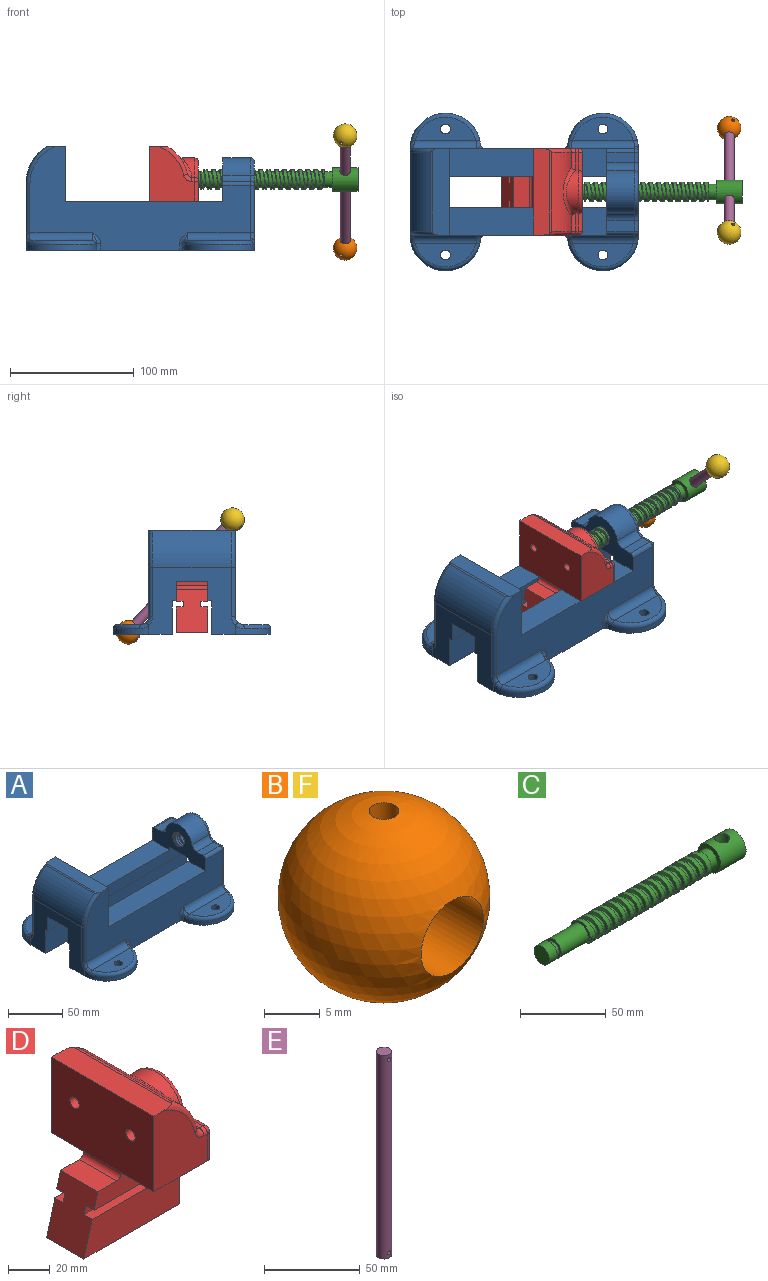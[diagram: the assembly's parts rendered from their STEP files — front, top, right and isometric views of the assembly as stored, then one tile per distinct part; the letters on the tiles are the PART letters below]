
ASSEMBLY  parts=6 mates=6
PART A: 90 faces, bbox 191.8x135.1x93.3 mm
  f0: plane 69.98x35.06mm, normal (-1,0,0), area 1390.7mm2, adj f1,f4,f6,f7,f9,f25,f26,f27
  f1: cylinder r=6.39mm len=25.4mm, axis (1,0,0), area 430.9mm2, adj f0,f5,f86,f88,f89
  f2: plane 184.15x47.6mm, normal (0,0,-1), area 5973.6mm2, adj f3,f5,f6,f11,f12,f14,f15,f29
  f3: plane 69.85x53.98mm, normal (-1,0,0), area 2224.7mm2, adj f2,f10,f11,f17,f24,f28,f29,f30
  f4: plane 127x22.2mm, normal (0,0,1), area 2819.3mm2, adj f0,f7,f23,f35
  f5: plane 71.56x69.98mm, normal (1,0,0), area 2448.5mm2, adj f1,f2,f10,f14,f20,f28,f29,f30
  f6: plane 181.19x87.52mm, normal (0,1,0), area 6838.3mm2, adj f0,f2,f8,f9,f23,f42,f45,f51
  f7: plane 181.19x87.52mm, normal (0,-1,0), area 6838.3mm2, adj f0,f4,f8,f10,f23,f43,f44,f46
  f8: plane 70.71x14.43mm, normal (0,0,1), area 942.4mm2, adj f6,f7,f23,f81,f83,f85
  f9: plane 127x22.2mm, normal (0,0,1), area 2819.3mm2, adj f0,f6,f23,f32
  f10: plane 184.15x47.6mm, normal (0,0,-1), area 5973.6mm2, adj f3,f5,f7,f17,f18,f20,f21,f28
  f11: cylinder r=28.57mm len=57.01mm, axis (0,0,-1), area 423.3mm2, adj f2,f3,f69,f71,f73,f75
  f12: cylinder r=3.96mm len=7.93mm, axis (0,0,-1), area 197.3mm2, adj f2,f13
  f13: plane 49.19x19.05mm, normal (0,0,1), area 644.9mm2, adj f12,f42,f73
  f14: cylinder r=28.57mm len=57.01mm, axis (0,0,-1), area 423.3mm2, adj f2,f5,f51,f56,f58,f60
  f15: cylinder r=3.96mm len=7.93mm, axis (0,0,-1), area 197.3mm2, adj f2,f16
  f16: plane 49.19x19.05mm, normal (0,0,1), area 644.9mm2, adj f15,f45,f58
  f17: cylinder r=28.57mm len=57.01mm, axis (0,0,-1), area 423.3mm2, adj f3,f10,f72,f76,f78,f80
  f18: cylinder r=3.96mm len=7.93mm, axis (0,0,-1), area 197.3mm2, adj f10,f19
  f19: plane 49.19x19.05mm, normal (0,0,1), area 644.9mm2, adj f18,f43,f78
  f20: cylinder r=28.57mm len=57.01mm, axis (0,0,-1), area 423.3mm2, adj f5,f10,f46,f48,f49,f50
  f21: cylinder r=3.96mm len=7.93mm, axis (0,0,-1), area 197.3mm2, adj f10,f22
  f22: plane 49.19x19.05mm, normal (0,0,1), area 644.9mm2, adj f21,f44,f49
  f23: plane 69.85x44.45mm, normal (1,0,0), area 2960.4mm2, adj f4,f6,f7,f8,f9,f32,f34,f35
  f24: cylinder r=34.92mm len=63.5mm, axis (0,-1,0), area 2251.5mm2, adj f3,f81,f83,f85
  f25: cylinder r=17.45mm len=34.2mm, axis (1,0,0), area 1062.5mm2, adj f0,f40,f41,f63
  f26: plane 22.23x8.43mm, normal (0,0,1), area 187.3mm2, adj f0,f41,f64,f68
  f27: plane 22.23x8.43mm, normal (0,0,1), area 187.3mm2, adj f0,f40,f55,f59
  f28: plane 184.15x26.97mm, normal (0,1,0), area 4967.4mm2, adj f3,f5,f10,f31
  f29: plane 184.15x26.97mm, normal (0,-1,0), area 4967.4mm2, adj f2,f3,f5,f30
  f30: plane 184.15x3.18mm, normal (0,0,-1), area 584.7mm2, adj f3,f5,f29,f32
  f31: plane 184.15x3.18mm, normal (0,0,-1), area 584.7mm2, adj f3,f5,f28,f35
  f32: plane 184.15x15.89mm, normal (0,-1,0), area 2520.9mm2, adj f0,f3,f5,f9,f23,f30,f33,f34
  f33: plane 25.45x25.4mm, normal (0,0,-1), area 646.5mm2, adj f0,f5,f32,f35
  f34: plane 31.75x25.45mm, normal (0,0,-1), area 808.1mm2, adj f3,f23,f32,f35
  f35: plane 184.15x15.89mm, normal (0,1,0), area 2520.9mm2, adj f0,f3,f4,f5,f23,f31,f33,f34
  f36: cylinder r=3.17mm len=15.88mm, axis (1,0,0), area 316.7mm2, adj f23,f37
  f37: plane 6.35x6.35mm, normal (1,0,0), area 31.7mm2, adj f36
  f38: cylinder r=3.17mm len=15.88mm, axis (1,0,0), area 316.7mm2, adj f23,f39
  f39: plane 6.35x6.35mm, normal (1,0,0), area 31.7mm2, adj f38
  f40: cylinder r=6.35mm len=22.23mm, axis (1,0,0), area 193.3mm2, adj f0,f25,f27,f61
  f41: cylinder r=6.35mm len=22.23mm, axis (1,0,0), area 193.3mm2, adj f0,f25,f26,f66
  f42: cylinder r=6.35mm len=50.6mm, axis (-1,0,0), area 499.8mm2, adj f6,f13,f71,f75,f77
  f43: cylinder r=6.35mm len=50.6mm, axis (1,0,0), area 499.8mm2, adj f7,f19,f76,f80,f82
  f44: cylinder r=6.35mm len=50.6mm, axis (1,0,0), area 499.8mm2, adj f7,f22,f48,f50,f52
  f45: cylinder r=6.35mm len=50.6mm, axis (-1,0,0), area 499.8mm2, adj f6,f16,f56,f60,f62
  f46: cylinder r=3.17mm len=5.55mm, axis (0,0,-1), area 25.9mm2, adj f7,f10,f20,f47
  f47: bspline ~10.3x6.39mm, area 17.6mm2, adj f7,f46,f48
  f48: bspline ~11.96x10.37mm, area 38.2mm2, adj f20,f44,f47,f49
  f49: torus R=25.4mm, axis (0,0,1), area 360.5mm2, adj f20,f22,f48,f50
  f50: bspline ~9.34x5.4mm, area 29.6mm2, adj f20,f44,f49,f52
  f51: cylinder r=3.17mm len=5.55mm, axis (0,0,-1), area 25.9mm2, adj f2,f6,f14,f53
  f52: torus R=9.53mm, axis (1,0,0), area 31.5mm2, adj f5,f44,f50,f54
  f53: bspline ~10.3x6.39mm, area 15.9mm2, adj f6,f51,f56
  f54: cylinder r=3.17mm len=38.1mm, axis (0,0,1), area 190mm2, adj f5,f7,f52,f57
  f55: cylinder r=3.17mm len=22.23mm, axis (-1,0,0), area 110.8mm2, adj f0,f7,f27,f57
  f56: bspline ~11.96x10.37mm, area 38.2mm2, adj f14,f45,f53,f58
  f57: sphere r=3.17mm, area 15.8mm2, adj f54,f55,f59
  f58: torus R=25.4mm, axis (0,0,1), area 360.5mm2, adj f14,f16,f56,f60
  f59: cylinder r=3.17mm len=8.43mm, axis (0,-1,0), area 42mm2, adj f5,f27,f57,f61
  f60: bspline ~9.34x5.4mm, area 29.6mm2, adj f14,f45,f58,f62
  f61: torus R=9.53mm, axis (1,0,0), area 51.3mm2, adj f5,f40,f59,f63
  f62: torus R=9.53mm, axis (1,0,0), area 31.5mm2, adj f5,f45,f60,f65
  f63: torus R=14.27mm, axis (1,0,0), area 222.7mm2, adj f5,f25,f61,f66
  f64: cylinder r=3.17mm len=22.23mm, axis (-1,0,0), area 110.8mm2, adj f0,f6,f26,f67
  f65: cylinder r=3.17mm len=38.1mm, axis (0,0,-1), area 190mm2, adj f5,f6,f62,f67
  f66: torus R=9.53mm, axis (1,0,0), area 51.3mm2, adj f5,f41,f63,f68
  f67: sphere r=3.17mm, area 10.1mm2, adj f64,f65,f68
  f68: cylinder r=3.17mm len=8.43mm, axis (0,-1,0), area 42mm2, adj f5,f26,f66,f67
  f69: cylinder r=3.17mm len=5.55mm, axis (0,0,-1), area 25.9mm2, adj f2,f6,f11,f70
  f70: bspline ~10.3x6.39mm, area 17.6mm2, adj f6,f69,f71
  f71: bspline ~11.96x10.37mm, area 38.2mm2, adj f11,f42,f70,f73
  f72: cylinder r=3.17mm len=5.55mm, axis (0,0,-1), area 25.9mm2, adj f7,f10,f17,f74
  f73: torus R=25.4mm, axis (0,0,1), area 360.5mm2, adj f11,f13,f71,f75
  f74: bspline ~10.3x6.39mm, area 15.9mm2, adj f7,f72,f76
  f75: bspline ~9.34x5.4mm, area 29.6mm2, adj f11,f42,f73,f77
  f76: bspline ~11.96x10.37mm, area 38.2mm2, adj f17,f43,f74,f78
  f77: torus R=9.53mm, axis (1,0,0), area 31.5mm2, adj f3,f42,f75,f79
  f78: torus R=25.4mm, axis (0,0,1), area 360.5mm2, adj f17,f19,f76,f80
  f79: cylinder r=3.17mm len=39.7mm, axis (0,0,1), area 198mm2, adj f3,f6,f77,f81
  f80: bspline ~9.34x5.4mm, area 29.6mm2, adj f17,f43,f78,f82
  f81: torus R=31.75mm, axis (0,1,0), area 187.9mm2, adj f6,f8,f24,f79,f83
  f82: torus R=9.53mm, axis (1,0,0), area 31.5mm2, adj f3,f43,f80,f84
  f83: cylinder r=3.17mm len=66.71mm, axis (0,-1,0), area 114.8mm2, adj f8,f24,f81,f85
  f84: cylinder r=3.17mm len=39.7mm, axis (0,0,-1), area 198mm2, adj f3,f7,f82,f85
  f85: torus R=31.75mm, axis (0,1,0), area 187.9mm2, adj f7,f8,f24,f83,f84
  f86: plane 1.76x1.55mm, normal (-0.13,-0.01,0.99), area 2.4mm2, adj f0,f1,f87,f89
  f87: cylinder r=7.94mm len=25.4mm, axis (-1,0,0), area 524.5mm2, adj f0,f5,f86,f88,f89
  f88: bspline ~26.93x18.32mm, area 290.1mm2, adj f0,f1,f5,f87
  f89: bspline ~24.81x18.34mm, area 272.9mm2, adj f1,f5,f86,f87
PART B: 5 faces, bbox 19.1x19.1x18.9 mm
  f0: sphere r=9.53mm, area 1077.6mm2, adj f1,f3,f4
  f1: cylinder r=3.96mm len=11.84mm, axis (0,-1,0), area 283.2mm2, adj f0,f2,f3,f4
  f2: plane 7.91x7.91mm, normal (0,-1,0), area 49.2mm2, adj f1
  f3: cylinder r=1.32mm len=5.7mm, axis (0,0,1), area 46.4mm2, adj f0,f1
  f4: cylinder r=1.32mm len=5.7mm, axis (0,0,1), area 46.4mm2, adj f0,f1
PART C: 21 faces, bbox 159.1x19.2x19.2 mm
  f0: cylinder r=9.53mm len=20.63mm, axis (-1,0,0), area 1111.2mm2, adj f18,f19,f20
  f1: plane 16.01x15.91mm, normal (1,0,0), area 53.5mm2, adj f2,f7,f8,f17
  f2: cylinder r=7.94mm len=100mm, axis (-1,0,0), area 3461mm2, adj f1,f3,f4,f6,f7,f8
  f3: plane 16.02x15.87mm, normal (-1,0,0), area 53.5mm2, adj f2,f4,f6,f10
  f4: plane 1.85x1.76mm, normal (0.13,0.01,-0.99), area 2.8mm2, adj f2,f3,f5,f8,f9
  f5: bspline ~103.1x14.08mm, area 1565.3mm2, adj f4,f6,f7,f8,f9,f16
  f6: bspline ~99.96x18.32mm, area 1318.7mm2, adj f2,f3,f5,f7,f9
  f7: plane 1.85x1.76mm, normal (-0.13,0.99,0), area 2.8mm2, adj f1,f2,f5,f6,f16
  f8: bspline ~99.96x18.34mm, area 1312.5mm2, adj f1,f2,f4,f5,f16
  f9: plane 6.27x5.25mm, normal (1,0,0), area 2.1mm2, adj f4,f5,f6,f10
  f10: cylinder r=6.35mm len=22.35mm, axis (1,0,0), area 891.8mm2, adj f3,f9,f11
  f11: plane 12.7x12.7mm, normal (-1,0,0), area 55.4mm2, adj f10,f12
  f12: cylinder r=4.76mm len=9.53mm, axis (1,0,0), area 98.8mm2, adj f11,f15
  f13: cylinder r=6.35mm len=12.7mm, axis (1,0,0), area 253.4mm2, adj f14,f15
  f14: plane 12.7x12.7mm, normal (-1,0,0), area 126.7mm2, adj f13
  f15: plane 12.7x12.7mm, normal (1,0,0), area 55.4mm2, adj f12,f13
  f16: plane 6.3x5.05mm, normal (-1,0,0), area 2.1mm2, adj f5,f7,f8,f17
  f17: cylinder r=6.35mm len=12.7mm, axis (-1,0,0), area 253.4mm2, adj f1,f16,f19
  f18: plane 19.05x19.05mm, normal (1,0,0), area 285mm2, adj f0
  f19: plane 19.05x19.05mm, normal (-1,0,0), area 158.3mm2, adj f0,f17
  f20: cylinder r=4.37mm len=19.05mm, axis (0,0,-1), area 522.6mm2, adj f0
PART D: 48 faces, bbox 65.9x70.7x89.2 mm
  f0: plane 14.38x2.42mm, normal (0,0,1), area 34.6mm2, adj f24,f32,f35,f37,f38
  f1: plane 70.71x14.43mm, normal (0,0,1), area 942.4mm2, adj f2,f4,f23,f36,f39,f42
  f2: plane 44.45x36.5mm, normal (0,1,0), area 1225.7mm2, adj f1,f17,f23,f42,f43,f45,f47
  f3: plane 69.82x63.5mm, normal (1,0,0), area 2160.8mm2, adj f5,f6,f7,f8,f9,f10,f11,f12
  f4: plane 44.45x36.5mm, normal (0,-1,0), area 1225.7mm2, adj f1,f5,f23,f31,f32,f33,f36
  f5: plane 39.68x22.23mm, normal (0,0,-1), area 879.6mm2, adj f3,f4,f6,f23,f31
  f6: plane 58.18x12.83mm, normal (0,-1,0), area 677mm2, adj f3,f5,f7,f20,f21,f22
  f7: plane 58.18x5.59mm, normal (0,0,-1), area 325.1mm2, adj f3,f6,f8,f20
  f8: plane 59.48x4.76mm, normal (0,-1,0), area 280.2mm2, adj f3,f7,f9,f20
  f9: plane 59.48x5.59mm, normal (0,0,1), area 332.4mm2, adj f3,f8,f10,f20
  f10: plane 65.08x20.51mm, normal (0,-1,0), area 1277.4mm2, adj f3,f9,f11,f20
  f11: plane 65.08x25.4mm, normal (0,0,-1), area 1652.9mm2, adj f3,f10,f12,f20
  f12: plane 65.08x20.51mm, normal (0,1,0), area 1277.4mm2, adj f3,f11,f13,f20
  f13: plane 59.48x5.59mm, normal (0,0,1), area 332.4mm2, adj f3,f12,f14,f20
  f14: plane 59.48x4.76mm, normal (0,1,0), area 280.2mm2, adj f3,f13,f15,f20
  f15: plane 58.18x5.59mm, normal (0,0,-1), area 325.1mm2, adj f3,f14,f16,f20
  f16: plane 58.18x12.83mm, normal (0,1,0), area 677mm2, adj f3,f15,f17,f20,f21,f22
  f17: plane 39.68x22.23mm, normal (0,0,-1), area 879.6mm2, adj f2,f3,f16,f23,f43
  f18: cylinder r=34.92mm len=63.5mm, axis (0,-1,0), area 1312.4mm2, adj f35,f36,f38,f39,f41,f42
  f19: plane 14.38x2.42mm, normal (0,0,1), area 34.6mm2, adj f24,f38,f41,f44,f47
  f20: plane 34.93x25.4mm, normal (-0.96,0,0.26), area 864.3mm2, adj f6,f7,f8,f9,f10,f11,f12,f13
  f21: plane 25.4x12.7mm, normal (0,0,1), area 322.6mm2, adj f6,f16,f20,f22
  f22: cylinder r=3.17mm len=25.4mm, axis (0,-1,0), area 126.7mm2, adj f6,f16,f21,f23
  f23: plane 69.85x44.45mm, normal (-1,0,0), area 3041.5mm2, adj f1,f2,f4,f5,f17,f22,f27,f29
  f24: cylinder r=17.45mm len=34.75mm, axis (1,0,0), area 319.6mm2, adj f0,f19,f38,f40
  f25: cylinder r=6.35mm len=30.15mm, axis (1,0,0), area 1202.9mm2, adj f3,f26
  f26: plane 12.7x12.7mm, normal (1,0,0), area 126.7mm2, adj f25
  f27: cylinder r=3.17mm len=15.88mm, axis (-1,0,0), area 316.7mm2, adj f23,f28
  f28: plane 6.35x6.35mm, normal (-1,0,0), area 31.7mm2, adj f27
  f29: cylinder r=3.17mm len=15.88mm, axis (-1,0,0), area 316.7mm2, adj f23,f30
  f30: plane 6.35x6.35mm, normal (-1,0,0), area 31.7mm2, adj f29
  f31: cylinder r=3.17mm len=15.88mm, axis (0,0,1), area 79.2mm2, adj f3,f4,f5,f34
  f32: cylinder r=3.17mm len=3.18mm, axis (1,0,0), area 12mm2, adj f0,f4,f33,f34
  f33: torus R=6.35mm, axis (0,1,0), area 29.4mm2, adj f4,f32,f35,f36
  f34: sphere r=3.17mm, area 15.8mm2, adj f31,f32,f37
  f35: cylinder r=3.17mm len=14.34mm, axis (0,-1,0), area 56.2mm2, adj f0,f18,f33,f38
  f36: torus R=31.75mm, axis (0,1,0), area 152.6mm2, adj f1,f4,f18,f33,f39
  f37: cylinder r=3.17mm len=17.56mm, axis (0,-1,0), area 79.6mm2, adj f0,f3,f34,f40
  f38: bspline ~41.25x18.62mm, area 206.8mm2, adj f0,f18,f19,f24,f35,f41
  f39: cylinder r=3.17mm len=66.71mm, axis (0,-1,0), area 114.8mm2, adj f1,f18,f36,f42
  f40: torus R=14.27mm, axis (1,0,0), area 256.3mm2, adj f3,f24,f37,f44
  f41: cylinder r=3.17mm len=14.34mm, axis (0,-1,0), area 56.2mm2, adj f18,f19,f38,f45
  f42: torus R=31.75mm, axis (0,1,0), area 152.6mm2, adj f1,f2,f18,f39,f45
  f43: cylinder r=3.17mm len=15.88mm, axis (0,0,-1), area 79.2mm2, adj f2,f3,f17,f46
  f44: cylinder r=3.17mm len=17.56mm, axis (0,-1,0), area 79.6mm2, adj f3,f19,f40,f46
  f45: torus R=6.35mm, axis (0,1,0), area 29.4mm2, adj f2,f41,f42,f47
  f46: sphere r=3.17mm, area 10.1mm2, adj f43,f44,f47
  f47: cylinder r=3.17mm len=3.18mm, axis (1,0,0), area 12mm2, adj f2,f19,f45,f46
PART E: 5 faces, bbox 7.9x7.9x130.2 mm
  f0: cylinder r=3.95mm len=130.18mm, axis (0,0,-1), area 3208.4mm2, adj f1,f2,f3,f4
  f1: plane 7.9x7.9mm, normal (0,0,1), area 49mm2, adj f0
  f2: plane 7.9x7.9mm, normal (0,0,-1), area 49mm2, adj f0
  f3: cylinder r=1.35mm len=7.9mm, axis (0,-1,0), area 65.1mm2, adj f0
  f4: cylinder r=1.28mm len=7.9mm, axis (0,-1,0), area 61.9mm2, adj f0
PART F: same geometry as B
PLACE A at identity fixed
PLACE B rot(axis=(-0.07,-0.91,0.4),162.1deg) t=(165.38,51.43,1.66)mm
PLACE C rot(axis=(-1,0,0),137.2deg) t=(48.72,0,57.15)mm
PLACE D t=(-18.21,2.12,31.01)mm
PLACE E rot(axis=(0.06,-0.36,0.93),161.8deg) t=(165.38,53.59,-0.67)mm
PLACE F rot(axis=(0.16,0.4,0.91),172.2deg) t=(165.38,-32.74,92.48)mm
MATE pin_slot C.f0 <-> D.f24  axis (-1,0,0) through (16.72,0,57.15)mm
MATE pin_slot A.f4 <-> D.f5  axis (0,0,1) through (-60.32,-34.93,39.67)mm
MATE fastened B.f1 <-> E.f0  axis (0,-0.68,0.73) through (165.38,53.59,-0.67)mm
MATE cylindrical A.f87 <-> C.f0  axis (1,0,0) through (66.68,0,57.15)mm
MATE cylindrical E.f0 <-> C.f20  axis (0,0.68,-0.73) through (165.38,9.34,47.07)mm
MATE fastened F.f1 <-> E.f0  axis (0,0.68,-0.73) through (165.38,-34.9,94.8)mm
